# Revit family: 54372207(2022)
name_source: partatom
category: Plumbing Fixtures
units: mm (PartAtom-declared; Revit-internal decimal feet)

## family parameters
Always vertical = Yes
Cut with Voids When Loaded = No
OmniClass Number = 23.45.55.00
OmniClass Title = Sanitary Faucets, Wastes
Part Type = Normal
Room Calculation Point = No
Round Connector Dimension = Use Diameter
Shared = No
Work Plane-Based = No

## types (3) — shared parameters
3D View = https://static.hansa.com
Advanced Features = Inner body made of DZR brass
Aerator = Standard aerator;PCA® - constant flow rate regardless of pressure variations
AssetType = Fixed
Backflow Prevention EN1717 = AA
BodyMaterial = Brass
Brand = HANSA
Catalog Drawing URL = http://static.hansa.com
Connection = Flexible inlet pipes
Connection Size = G3/8
Dimension Drawing URL = http://static.hansa.com
DurationUnit = Year
EN Standard = EN 817
Excluded Items = Without pop-up waste
FDV Document URL = http://www.hansa.com
Features = Single-lever
Finish = Polished
Flow Drawing URL = http://static.hansa.com
Flow Rate At 300kPa With Flow Controller = 0.0 L/s
Flow Rate At 300kPa With Flow Reducers = 0.0 L/s
Group = Washbasin faucet
IfcExportAs = IfcValveType
IfcExportType = FAUCET
InletConnectionSize = 10 mm  [stored 0.0328084 ft]
Installation Type = Deck mounted
Installation and Maintenance Guide URL = http://static.hansa.com
Interactive AR View URL = https://static.hansa.com
Lever Handle = Single operating lever/handle;Pin shape;Hot/Cold symbols
Manufacturer = HANSA
ManufacturerName = HANSA
ManufacturerURL = http://www.hansa.com
Material = Brass
Max. Hot Water Supply = 70 °C
Mechanical Parts = 30Cartridge
Mobile Product Information URL = http://mpi.hansa.com
Mounting Holes = 1 hole
NBSDescription = Water supply fittings for wash basins and troughs
NBSReference = 45-35-70/371
NominalDepth = 168 mm
NominalHeight = 198 mm
NominalWidth = 50 mm  [stored 0.164042 ft]
Product Family = HANSAVANTIS Style
Product Image URL = http://static.hansa.com
Product URL = http://static.hansa.com
Sales Package dimensions (LxWxH) = 380 x 180 x 74
Shape = Sculptured
Size = 50x170x200 mm
Spout Projection = 133 mm
Spout Type = Fixed spout
Technical DataSheet URL = http://www.hansa.com
Temperature Adjustments = Limitation option for maximum temperature and flow-rate
URL Declaration Of Performance (DOP) = http://static.hansa.com
URL Declaration of Asbestos = http://static.hansa.com
URL Declaration of Conformity = http://static.hansa.com
URL Declaration of SCIP = http://static.hansa.com
URL EU Packaging Declaration = http://static.hansa.com
URL EcoLabel Declaration = http://static.hansa.com
URL Materials Declaration = http://www.hansa.com
URL REACH = http://static.hansa.com
Uniclass2 = Pr_40_30_96_96
Uniclass2015Description = Washbasin manual water supply sets
Uniclass2015Reference = Pr_40_20_87_96
Version = 1
VersionDate = 20/02/2024
Warranty Information URL = http://warranty.hansa.com
WarrantyDescription = http://warranty.hansa.com
WarrantyDurationUnit = Year
zero-valued in all types: CloseOffRating, Default Elevation, FlowCoefficient

## per-type parameters (varying)
- 54372207 Washbasin faucet - Chrome: 2D/3D/BIM Files URL=http://static.hansa.com; BIMObjectName=54372207(2023); CO2 Emissions (A1-A3)=7.44; CO2 Emissions (A4)=0.21; CO2 Emissions (B7)=1854; CO2 Emissions (C2)=0.01; CO2 Emissions (C3)=0.02; CO2 Emissions (C4)=0.06; CO2 Emissions (D)=-5.29; Color=Chrome; EAN Number=4057304017414; ETIM Class Number=EC011328 Washbasin mixing tap; FaucetMainMaterial=Chrome; Market=International;Germany;Austria;Belgium;Netherlands;Czech Republic;Slovakia;Italy; Model=54372207 Washbasin faucet; ModelReference=54372207; Name=54372207 Washbasin faucet; Name_en=54372207 Washbasin faucet; Product Code=54372207; Spare-Part Information URL=http://static.hansa.com; Surface treatment=Chrome; Type=0; UNSPSC Class Number=30181700 Faucets or taps; URL Environmental Product Declaration EPD=http://www.hansa.com faucet.pdf; Working Pressure=50 - 1000 kPa
- 5437220780 Washbasin faucet - Brushed Steel: BIMObjectName=5437220780(2023); CO2 Emissions (A1-A3)=0; CO2 Emissions (A4)=0; CO2 Emissions (B7)=0; CO2 Emissions (C2)=0; CO2 Emissions (C3)=0; CO2 Emissions (C4)=0; CO2 Emissions (D)=0; Color=Brushed steel; EAN Number=4057304020421; FaucetMainMaterial=Brushed Steel; Model=5437220780 Washbasin faucet; ModelReference=5437220780; Name=5437220780 Washbasin faucet; Name_en=5437220780 Washbasin faucet; Noise Class=I (ISO 3822); Product Code=5437220780; Surface treatment=Brushed steel; Type=80; Working Pressure=50-1000 kPa
- 5437220781 Washbasin faucet - Brushed Bronze: BIMObjectName=5437220781(2023); CO2 Emissions (A1-A3)=0; CO2 Emissions (A4)=0; CO2 Emissions (B7)=0; CO2 Emissions (C2)=0; CO2 Emissions (C3)=0; CO2 Emissions (C4)=0; CO2 Emissions (D)=0; Color=BrushedBronze; EAN Number=4057304020438; FaucetMainMaterial=Brushed Bronze; Model=5437220781 Washbasin faucet; ModelReference=5437220781; Name=5437220781 Washbasin faucet; Name_en=5437220781 Washbasin faucet; Noise Class=I (ISO 3822); Product Code=5437220781; Surface treatment=BrushedBronze; Type=81; Working Pressure=50-1000 kPa

note: [stored X ft] marks values corroborated as IEEE doubles in the binary element streams (Revit-internal decimal feet)

## geometry (parser evidence)
native form markers: Sweep x5
no freeform markers — native parametric forms only
